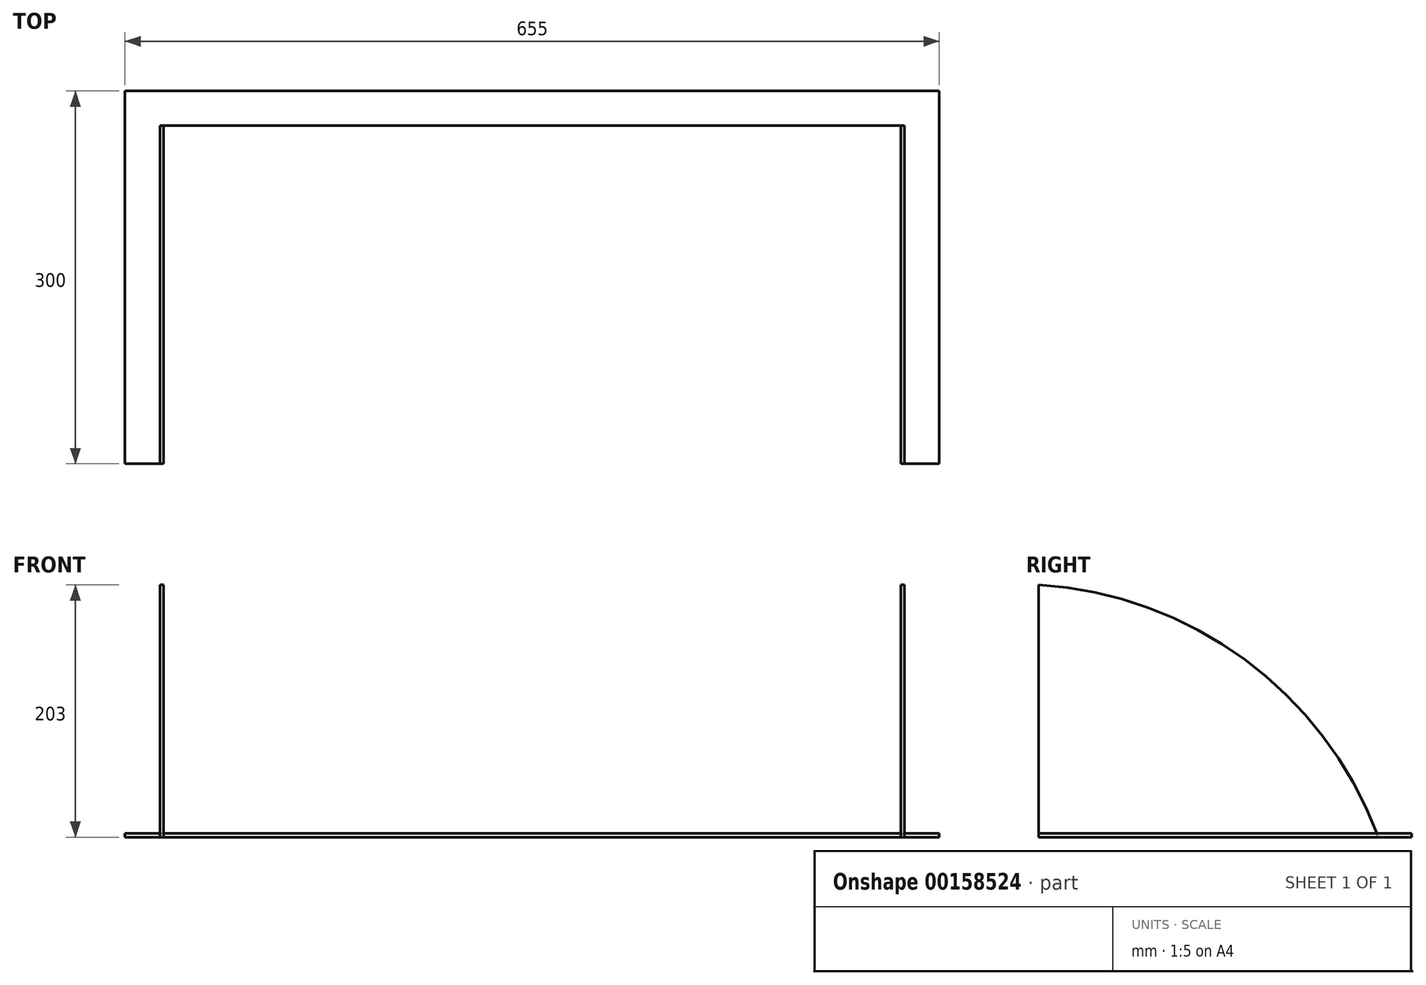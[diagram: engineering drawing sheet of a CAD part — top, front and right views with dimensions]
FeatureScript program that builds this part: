
annotation { "Feature Type Name" : "Feature", "Feature Type Description" : "" }
export const myFeature = defineFeature(function(context is Context, id is Id, definition is map)
    precondition{}
    {
        {
            var Q0;
            Q0=qCreatedBy(makeId("Top.planeOp"),FACE);
            var sketch = newSketch(context, id + "F0", { "sketchPlane" : qUnion([Q0])});
            skLineSegment(sketch, "E0.bottom", {"start": v(331.72, -227.5) * mm, "end": v(-323.28, -227.5) * mm});
            skLineSegment(sketch, "E0.top", {"start": v(331.72, 227.5) * mm, "end": v(-323.28, 227.5) * mm});
            skLineSegment(sketch, "E0.left", {"start": v(331.72, -227.5) * mm, "end": v(331.72, 227.5) * mm});
            skLineSegment(sketch, "E0.right", {"start": v(-323.28, -227.5) * mm, "end": v(-323.28, 227.5) * mm});
            skPoint(sketch, "E0.middle", {"position": v(4.22, 0) * mm});
            skLineSegment(sketch, "E1.0", {"start": v(-295.28, -199.5) * mm, "end": v(-295.28, 199.5) * mm});
            skLineSegment(sketch, "E1.1", {"start": v(303.72, -199.5) * mm, "end": v(-295.28, -199.5) * mm});
            skLineSegment(sketch, "E1.2", {"start": v(303.72, -199.5) * mm, "end": v(303.72, 199.5) * mm});
            skLineSegment(sketch, "E1.3", {"start": v(303.72, 199.5) * mm, "end": v(-295.28, 199.5) * mm});
            skLineSegment(sketch, "E2", {"start": v(331.72, 227.5) * mm, "end": v(331.72, -72.5) * mm, "construction": true});
            skLineSegment(sketch, "E3", {"start": v(331.72, -72.5) * mm, "end": v(-323.28, -72.5) * mm, "construction": true});
            skLineSegment(sketch, "E4", {"start": v(-323.28, -72.5) * mm, "end": v(-295.28, -72.5) * mm});
            skLineSegment(sketch, "E5", {"start": v(303.72, -72.5) * mm, "end": v(331.72, -72.5) * mm});
            skSolve(sketch);
        }
        {
            var Q0;
            {var subQ4=sQuery(id+"F0.wireOp",EDGE,"E0.top");Q0=makeQuery(id+"F0.imprint","IMPRINT",FACE,{"disambiguationData":[TD([[makeQuery(id+"F0.imprint","IMPRINT",EDGE,{"derivedFrom":subQ4}),1.0]])]});}
            extrude(context, id + "F1", {"entities" : qUnion([Q0]), "depth" : 3 * mm});
        }
        {
            var Q0;
            Q0=makeQuery(id+"F1.opExtrude","SWEPT_FACE",FACE,{"disambiguationData":[OSD([sQuery(id+"F0.wireOp",EDGE,"E1.0")])]});
            var sketch = newSketch(context, id + "F2", { "sketchPlane" : qUnion([Q0])});
            skLineSegment(sketch, "E6", {"start": v(-72.5, 3) * mm, "end": v(-72.5, 203) * mm});
            skArc(sketch, "E7", {"start": v(199.5, 3) * mm, "mid": v(92.96, 143.06) * mm, "end": v(-72.5, 203) * mm});
            skLineSegment(sketch, "E8.0", {"start": v(-72.5, 3) * mm, "end": v(-72.5, 0) * mm});
            skLineSegment(sketch, "E9.0", {"start": v(199.5, 3) * mm, "end": v(199.5, 0) * mm});
            skSolve(sketch);
        }
        {
            var Q0;
            Q0=makeQuery(id+"F2.imprint","IMPRINT",FACE,{"disambiguationData":[TD([[makeQuery(id+"F2.imprint","IMPRINT",EDGE,{"derivedFrom":sQuery(id+"F2.wireOp",EDGE,"E6")}),-1.0]])]});
            var Q1;
            Q1=makeQuery(id+"F2.imprint","IMPRINT",FACE,{"disambiguationData":[TD([[makeQuery(id+"F2.imprint","IMPRINT",EDGE,{"derivedFrom":sQuery(id+"F2.wireOp",EDGE,"E8.0")}),1.0]])]});
            extrude(context, id + "F3", {"entities" : qUnion([Q0, Q1]), "depth" : 3 * mm});
        }
        {
            var Q0;
            Q0=makeQuery(id+"F1.opExtrude","CAP_FACE",FACE,{"disambiguationData":[OSD([sQuery(id+"F0.wireOp",EDGE,"E0.top"),sQuery(id+"F0.wireOp",EDGE,"E0.left"),sQuery(id+"F0.wireOp",EDGE,"E0.right"),sQuery(id+"F0.wireOp",EDGE,"E1.0"),sQuery(id+"F0.wireOp",EDGE,"E1.2"),sQuery(id+"F0.wireOp",EDGE,"E1.3"),sQuery(id+"F0.wireOp",EDGE,"E4"),sQuery(id+"F0.wireOp",EDGE,"E5")])],"isStart":false});
            var sketch = newSketch(context, id + "F4", { "sketchPlane" : qUnion([Q0])});
            skLineSegment(sketch, "E10", {"start": v(4.22, 199.5) * mm, "end": v(4.22, 227.5) * mm});
            skSolve(sketch);
        }
        {
            var Q0;
            Q0=sQuery(id+"F4.wireOp",EDGE,"E10");
            cPlane(context, id + "F5", {"entities" : qUnion([Q0]), "cplaneType" : CPlaneType.LINE_ANGLE, "offset" : 25 * mm, "angle" : 90 * degree, "width" : 150 * mm, "height" : 150 * mm});
        }
        {
            var Q0;
            Q0=makeQuery(id+"F3.opExtrude","SWEPT_BODY",BODY,{"disambiguationData":[OSD([sQuery(id+"F0.wireOp",EDGE,"E1.0"),sQuery(id+"F2.wireOp",EDGE,"E6"),sQuery(id+"F2.wireOp",EDGE,"E7"),sQuery(id+"F2.wireOp",EDGE,"E8.0"),sQuery(id+"F2.wireOp",EDGE,"E9.0")])]});
            var Q1;
            Q1=qCreatedBy(id+"F5.planeOp",FACE);
            mirror(context, id + "F6", {"entities" : qUnion([Q0]), "mirrorPlane" : qUnion([Q1])});
        }
    });
